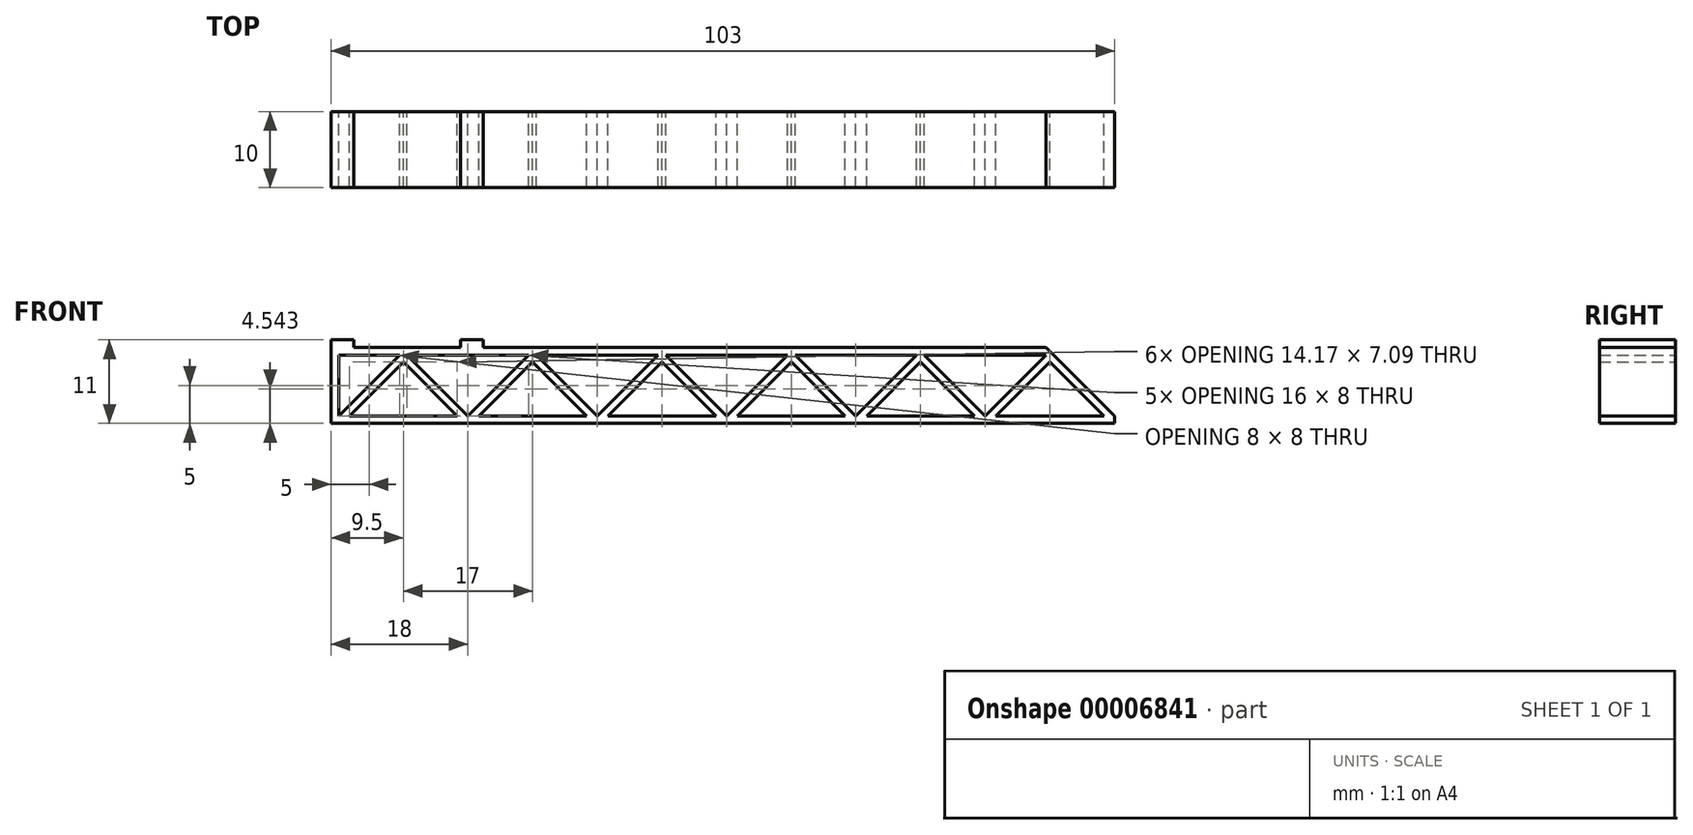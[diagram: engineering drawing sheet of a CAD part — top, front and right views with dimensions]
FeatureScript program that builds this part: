
annotation { "Feature Type Name" : "Feature", "Feature Type Description" : "" }
export const myFeature = defineFeature(function(context is Context, id is Id, definition is map)
    precondition{}
    {
        {
            var Q0;
            Q0=qCreatedBy(makeId("Front.planeOp"),FACE);
            var sketch = newSketch(context, id + "F0", { "sketchPlane" : qUnion([Q0])});
            skLineSegment(sketch, "E0.bottom", {"start": v(0, 0) * mm, "end": v(103, 0) * mm});
            skLineSegment(sketch, "E0.top", {"start": v(0, 10) * mm, "end": v(94, 10) * mm});
            skLineSegment(sketch, "E0.left", {"start": v(0, 0) * mm, "end": v(0, 10) * mm});
            skLineSegment(sketch, "E1", {"start": v(1, 9.5) * mm, "end": v(1, 1) * mm});
            skLineSegment(sketch, "E2", {"start": v(1, 1) * mm, "end": v(9.5, 9.5) * mm});
            skLineSegment(sketch, "E3", {"start": v(9.5, 9.5) * mm, "end": v(1, 9.5) * mm});
            skLineSegment(sketch, "E4", {"start": v(2.41, 1) * mm, "end": v(9.5, 1) * mm});
            skLineSegment(sketch, "E5", {"start": v(9.5, 8.09) * mm, "end": v(2.41, 1) * mm});
            skLineSegment(sketch, "E6", {"start": v(1, 1) * mm, "end": v(2.41, 1) * mm, "construction": true});
            skLineSegment(sketch, "E7", {"start": v(9.5, 9.5) * mm, "end": v(9.5, 1) * mm, "construction": true});
            skLineSegment(sketch, "E8.0.MirrorCS", {"start": v(16.59, 1) * mm, "end": v(9.5, 1) * mm});
            skLineSegment(sketch, "E9.0.MirrorCS", {"start": v(9.5, 8.09) * mm, "end": v(16.59, 1) * mm});
            skLineSegment(sketch, "E10.0.MirrorCS", {"start": v(18, 1) * mm, "end": v(9.5, 9.5) * mm});
            skLineSegment(sketch, "E11.0.MirrorCS", {"start": v(9.5, 9.5) * mm, "end": v(18, 9.5) * mm});
            skLineSegment(sketch, "E12", {"start": v(18, 9.5) * mm, "end": v(18, 1) * mm, "construction": true});
            skLineSegment(sketch, "E13.0.MirrorCS", {"start": v(18, 1) * mm, "end": v(26.5, 9.5) * mm});
            skLineSegment(sketch, "E14.0.MirrorCS", {"start": v(26.5, 8.09) * mm, "end": v(19.41, 1) * mm});
            skLineSegment(sketch, "E15.0.MirrorCS", {"start": v(35, 1) * mm, "end": v(26.5, 9.5) * mm});
            skLineSegment(sketch, "E16.0.MirrorCS", {"start": v(26.5, 8.09) * mm, "end": v(33.59, 1) * mm});
            skLineSegment(sketch, "E17.0.MirrorCS", {"start": v(33.59, 1) * mm, "end": v(26.5, 1) * mm});
            skLineSegment(sketch, "E18.0.MirrorCS", {"start": v(19.41, 1) * mm, "end": v(26.5, 1) * mm});
            skLineSegment(sketch, "E19.0.MirrorCS", {"start": v(26.5, 9.5) * mm, "end": v(18, 9.5) * mm});
            skLineSegment(sketch, "E20.0.MirrorCS", {"start": v(26.5, 9.5) * mm, "end": v(35, 9.5) * mm});
            skLineSegment(sketch, "E21.0.MirrorCS", {"start": v(26.5, 9.5) * mm, "end": v(26.5, 1) * mm, "construction": true});
            skLineSegment(sketch, "E22", {"start": v(35, 9.5) * mm, "end": v(35, 1) * mm, "construction": true});
            skLineSegment(sketch, "E23.0.MirrorCS", {"start": v(35, 1) * mm, "end": v(43.5, 9.5) * mm});
            skLineSegment(sketch, "E24.0.MirrorCS", {"start": v(43.5, 8.09) * mm, "end": v(36.41, 1) * mm});
            skLineSegment(sketch, "E25.0.MirrorCS", {"start": v(43.5, 8.09) * mm, "end": v(50.59, 1) * mm});
            skLineSegment(sketch, "E26.0.MirrorCS", {"start": v(52, 1) * mm, "end": v(43.5, 9.5) * mm});
            skLineSegment(sketch, "E27.0.MirrorCS", {"start": v(52, 1) * mm, "end": v(60.5, 9.5) * mm});
            skLineSegment(sketch, "E28.0.MirrorCS", {"start": v(60.5, 8.09) * mm, "end": v(53.41, 1) * mm});
            skLineSegment(sketch, "E29.0.MirrorCS", {"start": v(60.5, 8.09) * mm, "end": v(67.59, 1) * mm});
            skLineSegment(sketch, "E30.0.MirrorCS", {"start": v(69, 1) * mm, "end": v(60.5, 9.5) * mm});
            skLineSegment(sketch, "E31.0.MirrorCS", {"start": v(60.5, 9.5) * mm, "end": v(69, 9.5) * mm});
            skLineSegment(sketch, "E32.0.MirrorCS", {"start": v(60.5, 9.5) * mm, "end": v(52, 9.5) * mm});
            skLineSegment(sketch, "E33.0.MirrorCS", {"start": v(43.5, 9.5) * mm, "end": v(52, 9.5) * mm});
            skLineSegment(sketch, "E34.0.MirrorCS", {"start": v(43.5, 9.5) * mm, "end": v(35, 9.5) * mm});
            skLineSegment(sketch, "E35.0.MirrorCS", {"start": v(36.41, 1) * mm, "end": v(43.5, 1) * mm});
            skLineSegment(sketch, "E36.0.MirrorCS", {"start": v(50.59, 1) * mm, "end": v(43.5, 1) * mm});
            skLineSegment(sketch, "E37.0.MirrorCS", {"start": v(53.41, 1) * mm, "end": v(60.5, 1) * mm});
            skLineSegment(sketch, "E38.0.MirrorCS", {"start": v(67.59, 1) * mm, "end": v(60.5, 1) * mm});
            skLineSegment(sketch, "E39", {"start": v(69, 9.5) * mm, "end": v(69, 1) * mm, "construction": true});
            skLineSegment(sketch, "E40.0.MirrorCS", {"start": v(69, 1) * mm, "end": v(77.5, 9.5) * mm});
            skLineSegment(sketch, "E41.0.MirrorCS", {"start": v(77.5, 8.09) * mm, "end": v(70.41, 1) * mm});
            skLineSegment(sketch, "E42.0.MirrorCS", {"start": v(86, 1) * mm, "end": v(77.5, 9.5) * mm});
            skLineSegment(sketch, "E43.0.MirrorCS", {"start": v(77.5, 8.09) * mm, "end": v(84.59, 1) * mm});
            skLineSegment(sketch, "E44.0.MirrorCS", {"start": v(86, 1) * mm, "end": v(94.5, 9.5) * mm});
            skLineSegment(sketch, "E45.0.MirrorCS", {"start": v(94.5, 8.09) * mm, "end": v(87.41, 1) * mm});
            skLineSegment(sketch, "E46.0.MirrorCS", {"start": v(103, 1) * mm, "end": v(94.5, 9.5) * mm});
            skLineSegment(sketch, "E47.0.MirrorCS", {"start": v(94.5, 8.09) * mm, "end": v(101.59, 1) * mm});
            skLineSegment(sketch, "E48.0.MirrorCS", {"start": v(94.5, 9.5) * mm, "end": v(86, 9.5) * mm});
            skLineSegment(sketch, "E49.0.MirrorCS", {"start": v(77.5, 9.5) * mm, "end": v(86, 9.5) * mm});
            skLineSegment(sketch, "E50.0.MirrorCS", {"start": v(77.5, 9.5) * mm, "end": v(69, 9.5) * mm});
            skLineSegment(sketch, "E51.0.MirrorCS", {"start": v(70.41, 1) * mm, "end": v(77.5, 1) * mm});
            skLineSegment(sketch, "E52.0.MirrorCS", {"start": v(84.59, 1) * mm, "end": v(77.5, 1) * mm});
            skLineSegment(sketch, "E53.0.MirrorCS", {"start": v(87.41, 1) * mm, "end": v(94.5, 1) * mm});
            skLineSegment(sketch, "E54.0.MirrorCS", {"start": v(101.59, 1) * mm, "end": v(94.5, 1) * mm});
            skLineSegment(sketch, "E55", {"start": v(1, 9) * mm, "end": v(95, 9) * mm});
            skPoint(sketch, "E56.start.orphan", {"position": v(103, 9.5) * mm});
            skLineSegment(sketch, "E57", {"start": v(103, 0) * mm, "end": v(103, 1) * mm});
            skLineSegment(sketch, "E58", {"start": v(94.5, 9.5) * mm, "end": v(94, 10) * mm});
            skSolve(sketch);
        }
        {
            var Q0;
            Q0=makeQuery(id+"F0.imprint","IMPRINT",FACE,{"disambiguationData":[TD([[makeQuery(id+"F0.imprint","IMPRINT",EDGE,{"derivedFrom":sQuery(id+"F0.wireOp",EDGE,"E0.bottom")}),1.0]])]});
            var Q1;
            {var subQ5=sQuery(id+"F0.wireOp",EDGE,"E3");Q1=makeQuery(id+"F0.imprint","IMPRINT",FACE,{"disambiguationData":[TD([[makeQuery(id+"F0.imprint","IMPRINT",EDGE,{"derivedFrom":subQ5}),1.0]])]});}
            var Q2;
            {var subQ0=sQuery(id+"F0.wireOp",EDGE,"E55");var subQ3=sQuery(id+"F0.wireOp",EDGE,"E2");var subQ4=makeQuery(id+"F0.imprint","INTERSECT",VERTEX,{"derivedFrom":[subQ3,subQ0]});Q2=makeQuery(id+"F0.imprint","IMPRINT",FACE,{"disambiguationData":[TD([[makeQuery(id+"F0.imprint","IMPRINT",EDGE,{"disambiguationData":[TD([[subQ4,-1.0]])],"derivedFrom":subQ0}),1.0]])]});}
            var Q3;
            {var subQ6=sQuery(id+"F0.wireOp",EDGE,"E11.0.MirrorCS");Q3=makeQuery(id+"F0.imprint","IMPRINT",FACE,{"disambiguationData":[TD([[makeQuery(id+"F0.imprint","IMPRINT",EDGE,{"derivedFrom":subQ6}),-1.0]])]});}
            var Q4;
            {var subQ4=sQuery(id+"F0.wireOp",EDGE,"E20.0.MirrorCS");Q4=makeQuery(id+"F0.imprint","IMPRINT",FACE,{"disambiguationData":[TD([[makeQuery(id+"F0.imprint","IMPRINT",EDGE,{"derivedFrom":subQ4}),-1.0]])]});}
            var Q5;
            {var subQ0=sQuery(id+"F0.wireOp",EDGE,"E55");var subQ3=sQuery(id+"F0.wireOp",EDGE,"E13.0.MirrorCS");var subQ4=makeQuery(id+"F0.imprint","INTERSECT",VERTEX,{"derivedFrom":[subQ3,subQ0]});Q5=makeQuery(id+"F0.imprint","IMPRINT",FACE,{"disambiguationData":[TD([[makeQuery(id+"F0.imprint","IMPRINT",EDGE,{"disambiguationData":[TD([[subQ4,-1.0]])],"derivedFrom":subQ0}),1.0]])]});}
            var Q6;
            {var subQ0=sQuery(id+"F0.wireOp",EDGE,"E55");var subQ3=sQuery(id+"F0.wireOp",EDGE,"E23.0.MirrorCS");var subQ4=makeQuery(id+"F0.imprint","INTERSECT",VERTEX,{"derivedFrom":[subQ3,subQ0]});Q6=makeQuery(id+"F0.imprint","IMPRINT",FACE,{"disambiguationData":[TD([[makeQuery(id+"F0.imprint","IMPRINT",EDGE,{"disambiguationData":[TD([[subQ4,-1.0]])],"derivedFrom":subQ0}),1.0]])]});}
            var Q7;
            {var subQ6=sQuery(id+"F0.wireOp",EDGE,"E32.0.MirrorCS");Q7=makeQuery(id+"F0.imprint","IMPRINT",FACE,{"disambiguationData":[TD([[makeQuery(id+"F0.imprint","IMPRINT",EDGE,{"derivedFrom":subQ6}),1.0]])]});}
            var Q8;
            {var subQ5=sQuery(id+"F0.wireOp",EDGE,"4faee000-dc11-4320-abb4-952d76e3175e.0.MirrorCS");Q8=makeQuery(id+"F0.imprint","IMPRINT",FACE,{"disambiguationData":[TD([[makeQuery(id+"F0.imprint","IMPRINT",EDGE,{"derivedFrom":subQ5}),-1.0]])]});}
            var Q9;
            {var subQ0=sQuery(id+"F0.wireOp",EDGE,"E55");var subQ3=sQuery(id+"F0.wireOp",EDGE,"E44.0.MirrorCS");var subQ4=makeQuery(id+"F0.imprint","INTERSECT",VERTEX,{"derivedFrom":[subQ3,subQ0]});Q9=makeQuery(id+"F0.imprint","IMPRINT",FACE,{"disambiguationData":[TD([[makeQuery(id+"F0.imprint","IMPRINT",EDGE,{"disambiguationData":[TD([[subQ4,-1.0]])],"derivedFrom":subQ0}),1.0]])]});}
            var Q10;
            {var subQ6=sQuery(id+"F0.wireOp",EDGE,"E48.0.MirrorCS");Q10=makeQuery(id+"F0.imprint","IMPRINT",FACE,{"disambiguationData":[TD([[makeQuery(id+"F0.imprint","IMPRINT",EDGE,{"derivedFrom":subQ6}),1.0]])]});}
            var Q11;
            {var subQ6=sQuery(id+"F0.wireOp",EDGE,"E31.0.MirrorCS");Q11=makeQuery(id+"F0.imprint","IMPRINT",FACE,{"disambiguationData":[TD([[makeQuery(id+"F0.imprint","IMPRINT",EDGE,{"derivedFrom":subQ6}),-1.0]])]});}
            var Q12;
            {var subQ0=sQuery(id+"F0.wireOp",EDGE,"E55");var subQ3=sQuery(id+"F0.wireOp",EDGE,"E40.0.MirrorCS");var subQ4=makeQuery(id+"F0.imprint","INTERSECT",VERTEX,{"derivedFrom":[subQ3,subQ0]});Q12=makeQuery(id+"F0.imprint","IMPRINT",FACE,{"disambiguationData":[TD([[makeQuery(id+"F0.imprint","IMPRINT",EDGE,{"disambiguationData":[TD([[subQ4,-1.0]])],"derivedFrom":subQ0}),1.0]])]});}
            var Q13;
            {var subQ0=sQuery(id+"F0.wireOp",EDGE,"E55");var subQ3=sQuery(id+"F0.wireOp",EDGE,"E27.0.MirrorCS");var subQ4=makeQuery(id+"F0.imprint","INTERSECT",VERTEX,{"derivedFrom":[subQ3,subQ0]});Q13=makeQuery(id+"F0.imprint","IMPRINT",FACE,{"disambiguationData":[TD([[makeQuery(id+"F0.imprint","IMPRINT",EDGE,{"disambiguationData":[TD([[subQ4,-1.0]])],"derivedFrom":subQ0}),1.0]])]});}
            extrude(context, id + "F1", {"entities" : qUnion([Q0, Q1, Q2, Q3, Q4, Q5, Q6, Q7, Q8, Q9, Q10, Q11, Q12, Q13]), "depth" : 10 * mm});
        }
        {
            var Q0;
            Q0=makeQuery(id+"F1.opExtrude","SWEPT_FACE",FACE,{"disambiguationData":[OSD([sQuery(id+"F0.wireOp",EDGE,"E0.top")])]});
            var sketch = newSketch(context, id + "F2", { "sketchPlane" : qUnion([Q0])});
            skLineSegment(sketch, "E59.bottom", {"start": v(0, -10) * mm, "end": v(3, -10) * mm});
            skLineSegment(sketch, "E59.top", {"start": v(0, 0) * mm, "end": v(3, 0) * mm});
            skLineSegment(sketch, "E59.left", {"start": v(0, -10) * mm, "end": v(0, 0) * mm});
            skLineSegment(sketch, "E59.right", {"start": v(3, -10) * mm, "end": v(3, 0) * mm});
            skLineSegment(sketch, "E60.bottom", {"start": v(17, 0) * mm, "end": v(20, 0) * mm});
            skLineSegment(sketch, "E60.top", {"start": v(17, -10) * mm, "end": v(20, -10) * mm});
            skLineSegment(sketch, "E60.left", {"start": v(17, 0) * mm, "end": v(17, -10) * mm});
            skLineSegment(sketch, "E60.right", {"start": v(20, 0) * mm, "end": v(20, -10) * mm});
            skSolve(sketch);
        }
        {
            var Q0;
            Q0 = qSketchRegion(id + "F2", true);
            extrude(context, id + "F3", {"entities" : qUnion([Q0]), "operationType" : NewBodyOperationType.ADD, "depth" : 1 * mm});
        }
    });
